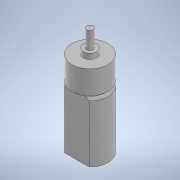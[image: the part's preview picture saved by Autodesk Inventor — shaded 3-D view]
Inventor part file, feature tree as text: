
AUTODESK INVENTOR PART (.ipt)
format: ipt  version: 2022 (Build 260153000, 153)  size: 136,192 bytes
history: native  units: in
note: dims shown in document units (in); Inventor stores cm internally (conversion verified against a paired STEP export)
features: sketch x2, revolve x1, extrude x1
ambient origin geometry x8: Origin, YZ Plane, XZ Plane, XY Plane, X Axis, Y Axis, Z Axis, Center Point
bodies: Body1 (feature_tree)
feature tree (4):
  revolve  "Revolution2"  [1 undecoded]
  extrude  "Extrusion5"  Depth=0.4606in
  sketch  "Sketch6"  dims[d31=0.6299in d32=0.1181in]
  sketch  "Sketch7"  dims[d34=360.0deg d35=0.0394in d36=0.4433in d38=1.0354in d39=0.0937in d40=0.2343in d41=0.3012in d42=0.4606in d43=1.0354in d44=0.0in]
note: 1 required parameter value undecoded (feature->parameter linkage not recoverable at this tier; creation-order binding heuristic only, values carry confidence <= 0.55)
